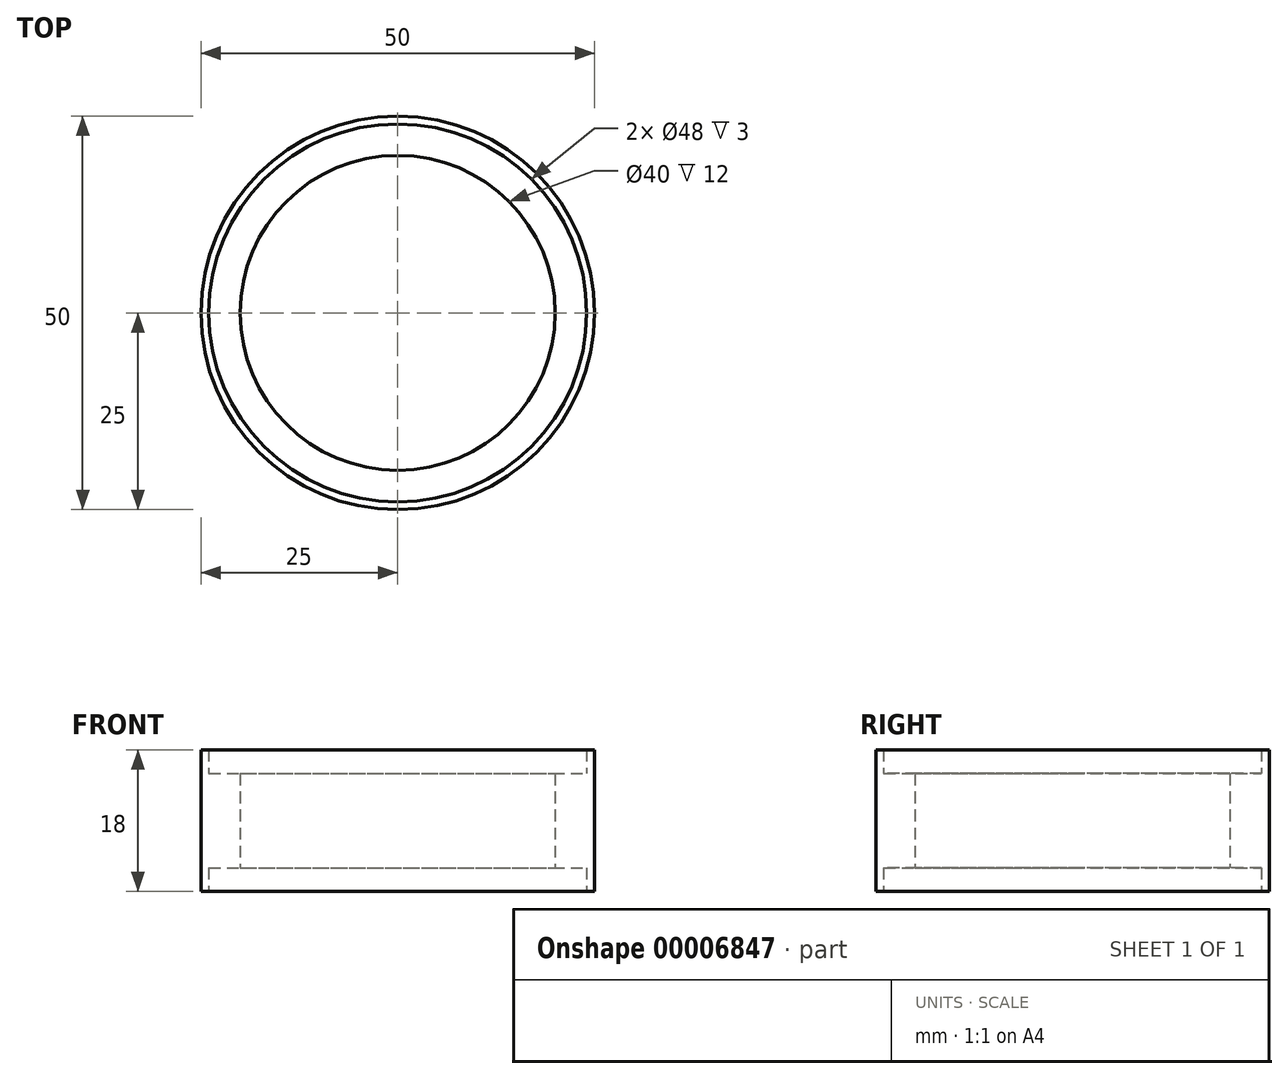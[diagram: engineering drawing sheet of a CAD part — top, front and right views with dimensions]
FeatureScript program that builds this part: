
annotation { "Feature Type Name" : "Feature", "Feature Type Description" : "" }
export const myFeature = defineFeature(function(context is Context, id is Id, definition is map)
    precondition{}
    {
        {
            var Q0;
            Q0=qCreatedBy(makeId("Front.planeOp"),FACE);
            var sketch = newSketch(context, id + "F0", { "sketchPlane" : qUnion([Q0])});
            skLineSegment(sketch, "E0", {"start": v(-25, 0) * mm, "end": v(-25, 18) * mm});
            skLineSegment(sketch, "E1", {"start": v(-25, 18) * mm, "end": v(-24, 18) * mm});
            skLineSegment(sketch, "E2", {"start": v(-24, 18) * mm, "end": v(-24, 15) * mm});
            skLineSegment(sketch, "E3", {"start": v(-24, 15) * mm, "end": v(-20, 15) * mm});
            skLineSegment(sketch, "E4", {"start": v(-20, 15) * mm, "end": v(-20, 3) * mm});
            skLineSegment(sketch, "E5", {"start": v(-20, 3) * mm, "end": v(-24, 3) * mm});
            skLineSegment(sketch, "E6", {"start": v(-24, 3) * mm, "end": v(-24, 0) * mm});
            skLineSegment(sketch, "E7", {"start": v(-24, 0) * mm, "end": v(-25, 0) * mm});
            skLineSegment(sketch, "E8", {"start": v(0, 0) * mm, "end": v(0, 20.04) * mm, "construction": true});
            skSolve(sketch);
        }
        {
            var Q0;
            Q0=makeQuery(id+"F0.imprint","IMPRINT",FACE,{"disambiguationData":[TD([[makeQuery(id+"F0.imprint","IMPRINT",EDGE,{"derivedFrom":sQuery(id+"F0.wireOp",EDGE,"E0")}),-1.0]])]});
            var Q1;
            Q1=sQuery(id+"F0.wireOp",EDGE,"E8");
            revolve(context, id + "F1", {"entities" : qUnion([Q0]), "axis" : qUnion([Q1]), "revolveType" : RevolveType.FULL});
        }
    });
